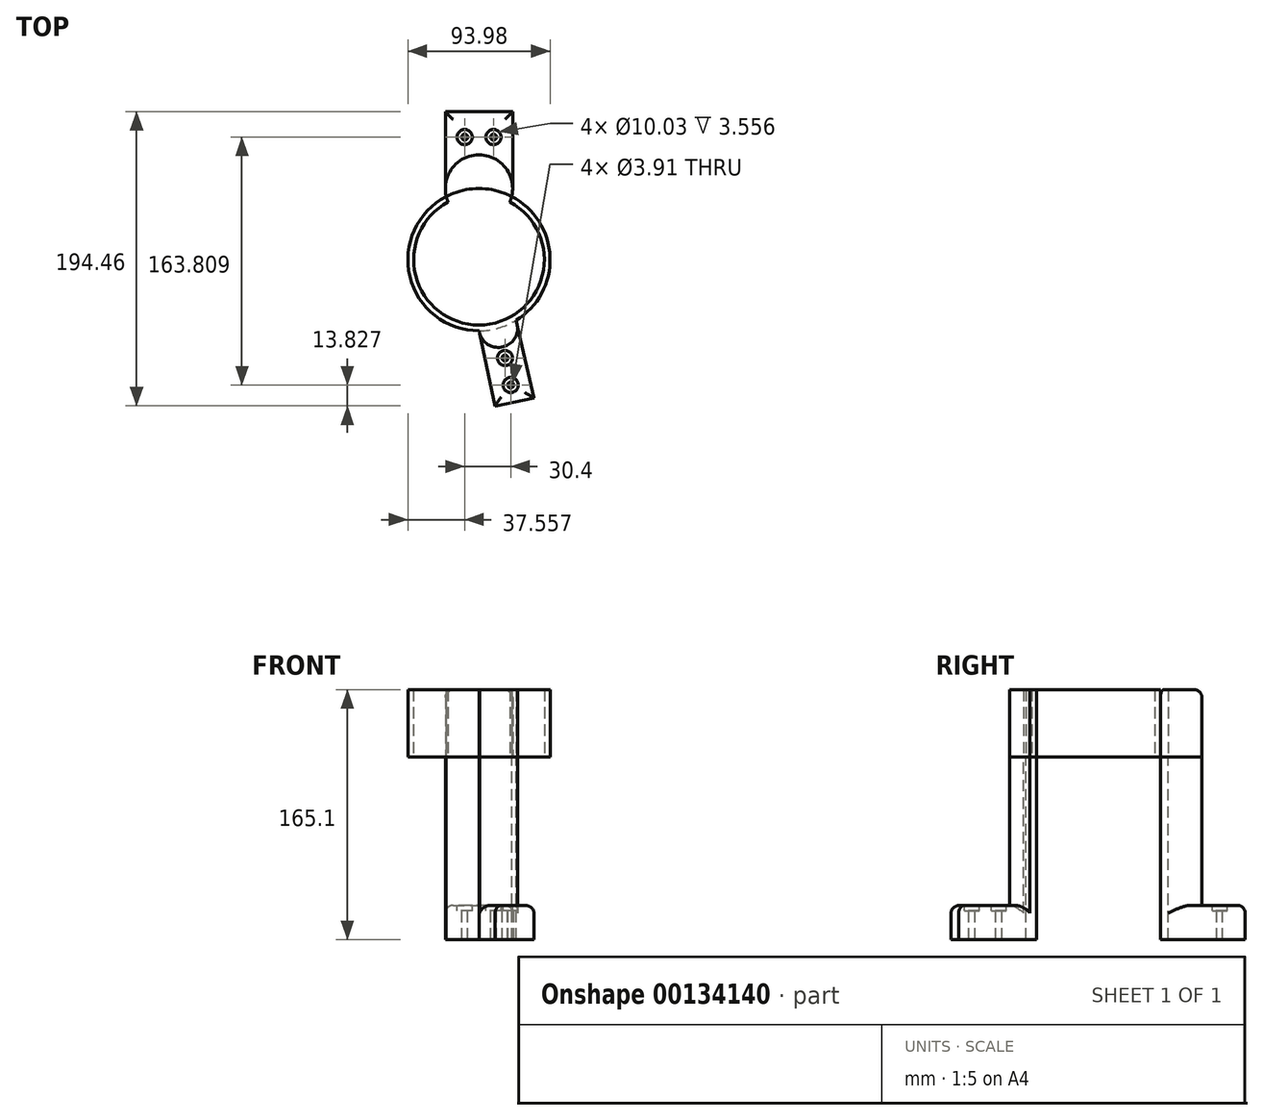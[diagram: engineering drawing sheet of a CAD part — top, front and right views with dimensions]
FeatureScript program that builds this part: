
annotation { "Feature Type Name" : "Feature", "Feature Type Description" : "" }
export const myFeature = defineFeature(function(context is Context, id is Id, definition is map)
    precondition{}
    {
        {
            var Q0;
            Q0=qCreatedBy(makeId("Top.planeOp"),FACE);
            var sketch = newSketch(context, id + "F0", { "sketchPlane" : qUnion([Q0])});
            skCircle(sketch, "E0", {"center": v(0, 0) * mm, "radius": 43.18 * mm});
            skCircle(sketch, "E1", {"center": v(0, 0) * mm, "radius": 47 * mm});
            skArc(sketch, "E2", {"start": v(0.07, -46.99) * mm, "mid": v(16.21, -57.54) * mm, "end": v(24.47, -40.11) * mm});
            skPoint(sketch, "E3.center.orphan", {"position": v(0, 47) * mm});
            skArc(sketch, "E4", {"start": v(0.12, -43.18) * mm, "mid": v(16.21, -57.54) * mm, "end": v(22.45, -36.89) * mm});
            skLineSegment(sketch, "E5", {"start": v(0.07, -46.99) * mm, "end": v(10.67, -96.67) * mm});
            skLineSegment(sketch, "E6", {"start": v(36.38, -91.59) * mm, "end": v(24.47, -40.11) * mm});
            skArc(sketch, "E7", {"start": v(20.36, 38.08) * mm, "mid": v(0, 69.22) * mm, "end": v(-20.36, 38.08) * mm});
            skLineSegment(sketch, "E8", {"start": v(-22.23, 47) * mm, "end": v(-22.23, 97.8) * mm});
            skLineSegment(sketch, "E9", {"start": v(-22.23, 97.8) * mm, "end": v(22.23, 97.8) * mm});
            skLineSegment(sketch, "E10", {"start": v(22.23, 97.8) * mm, "end": v(22.22, 46.99) * mm});
            skLineSegment(sketch, "E11", {"start": v(10.67, -96.67) * mm, "end": v(36.38, -91.59) * mm});
            skCircle(sketch, "E12", {"center": v(17.2, -64.98) * mm, "radius": 5.02 * mm});
            skCircle(sketch, "E13", {"center": v(20.97, -82.84) * mm, "radius": 5.02 * mm});
            skCircle(sketch, "E14", {"center": v(-9.43, 80.97) * mm, "radius": 5.02 * mm});
            skCircle(sketch, "E15.1.0.0", {"center": v(9.62, 80.97) * mm, "radius": 5.02 * mm});
            skLineSegment(sketch, "E15.direction1", {"start": v(-9.43, 80.97) * mm, "end": v(9.62, 80.97) * mm, "construction": true});
            skCircle(sketch, "E16", {"center": v(-9.43, 80.97) * mm, "radius": 1.96 * mm});
            skCircle(sketch, "E17", {"center": v(9.62, 80.97) * mm, "radius": 1.96 * mm});
            skCircle(sketch, "E18", {"center": v(17.2, -64.98) * mm, "radius": 1.96 * mm});
            skCircle(sketch, "E19", {"center": v(20.97, -82.84) * mm, "radius": 1.96 * mm});
            skSolve(sketch);
        }
        {
            var Q0;
            {var subQ0=sQuery(id+"F0.wireOp",EDGE,"E4");var subQ1=sQuery(id+"F0.wireOp",EDGE,"E1");var subQ2=makeQuery(id+"F0.imprint","INTERSECT",VERTEX,{"disambiguationData":[OD(0.0)],"derivedFrom":[subQ1,subQ0]});Q0=makeQuery(id+"F0.imprint","IMPRINT",FACE,{"disambiguationData":[TD([[makeQuery(id+"F0.imprint","IMPRINT",EDGE,{"disambiguationData":[TD([[subQ2,-1.0]])],"derivedFrom":subQ1}),-1.0]])]});}
            var Q1;
            {var subQ0=sQuery(id+"F0.wireOp",EDGE,"XKigaTq3-lD6u-q0mf-ILFs-nLOiHahSTtli");var subQ1=sQuery(id+"F0.wireOp",EDGE,"E1");var subQ2=makeQuery(id+"F0.imprint","INTERSECT",VERTEX,{"disambiguationData":[OD(0.0)],"derivedFrom":[subQ1,subQ0]});Q1=makeQuery(id+"F0.imprint","IMPRINT",FACE,{"disambiguationData":[TD([[makeQuery(id+"F0.imprint","IMPRINT",EDGE,{"disambiguationData":[TD([[subQ2,1.0]])],"derivedFrom":subQ1}),-1.0]])]});}
            extrude(context, id + "F1", {"entities" : qUnion([Q0, Q1]), "oppositeDirection" : true, "depth" : 120.65 * mm});
        }
        {
            var Q0;
            {var subQ0=sQuery(id+"F0.wireOp",EDGE,"E4");var subQ1=sQuery(id+"F0.wireOp",EDGE,"E0");var subQ2=makeQuery(id+"F0.imprint","INTERSECT",VERTEX,{"disambiguationData":[OD(1.0)],"derivedFrom":[subQ1,subQ0]});Q0=makeQuery(id+"F0.imprint","IMPRINT",FACE,{"disambiguationData":[TD([[makeQuery(id+"F0.imprint","IMPRINT",EDGE,{"disambiguationData":[TD([[subQ2,-1.0]])],"derivedFrom":subQ1}),-1.0]])]});}
            var Q1;
            {var subQ0=sQuery(id+"F0.wireOp",EDGE,"E4");var subQ1=sQuery(id+"F0.wireOp",EDGE,"E0");var subQ2=makeQuery(id+"F0.imprint","INTERSECT",VERTEX,{"disambiguationData":[OD(0.0)],"derivedFrom":[subQ1,subQ0]});Q1=makeQuery(id+"F0.imprint","IMPRINT",FACE,{"disambiguationData":[TD([[makeQuery(id+"F0.imprint","IMPRINT",EDGE,{"disambiguationData":[TD([[subQ2,-1.0]])],"derivedFrom":subQ1}),-1.0]])]});}
            var Q2;
            {var subQ0=sQuery(id+"F0.wireOp",EDGE,"E4");var subQ1=sQuery(id+"F0.wireOp",EDGE,"E0");var subQ2=makeQuery(id+"F0.imprint","INTERSECT",VERTEX,{"disambiguationData":[OD(0.0)],"derivedFrom":[subQ1,subQ0]});Q2=makeQuery(id+"F0.imprint","IMPRINT",FACE,{"disambiguationData":[TD([[makeQuery(id+"F0.imprint","IMPRINT",EDGE,{"disambiguationData":[TD([[subQ2,1.0]])],"derivedFrom":subQ1}),-1.0]])]});}
            var Q3;
            {var subQ0=sQuery(id+"F0.wireOp",EDGE,"XKigaTq3-lD6u-q0mf-ILFs-nLOiHahSTtli");var subQ1=sQuery(id+"F0.wireOp",EDGE,"E0");var subQ2=makeQuery(id+"F0.imprint","INTERSECT",VERTEX,{"disambiguationData":[OD(0.0)],"derivedFrom":[subQ1,subQ0]});Q3=makeQuery(id+"F0.imprint","IMPRINT",FACE,{"disambiguationData":[TD([[makeQuery(id+"F0.imprint","IMPRINT",EDGE,{"disambiguationData":[TD([[subQ2,-1.0]])],"derivedFrom":subQ1}),-1.0]])]});}
            var Q4;
            {var subQ0=sQuery(id+"F0.wireOp",EDGE,"XKigaTq3-lD6u-q0mf-ILFs-nLOiHahSTtli");var subQ1=sQuery(id+"F0.wireOp",EDGE,"E1");var subQ2=makeQuery(id+"F0.imprint","INTERSECT",VERTEX,{"disambiguationData":[OD(0.0)],"derivedFrom":[subQ1,subQ0]});Q4=makeQuery(id+"F0.imprint","IMPRINT",FACE,{"disambiguationData":[TD([[makeQuery(id+"F0.imprint","IMPRINT",EDGE,{"disambiguationData":[TD([[subQ2,1.0]])],"derivedFrom":subQ1}),-1.0]])]});}
            var Q5;
            {var subQ0=sQuery(id+"F0.wireOp",EDGE,"E4");var subQ1=sQuery(id+"F0.wireOp",EDGE,"E1");var subQ2=makeQuery(id+"F0.imprint","INTERSECT",VERTEX,{"disambiguationData":[OD(0.0)],"derivedFrom":[subQ1,subQ0]});Q5=makeQuery(id+"F0.imprint","IMPRINT",FACE,{"disambiguationData":[TD([[makeQuery(id+"F0.imprint","IMPRINT",EDGE,{"disambiguationData":[TD([[subQ2,-1.0]])],"derivedFrom":subQ1}),-1.0]])]});}
            extrude(context, id + "F2", {"entities" : qUnion([Q0, Q1, Q2, Q3, Q4, Q5]), "depth" : 44.45 * mm});
        }
        {
            var Q0;
            {var subQ0=sQuery(id+"F0.wireOp",EDGE,"E11");Q0=makeQuery(id+"F0.imprint","IMPRINT",FACE,{"disambiguationData":[TD([[makeQuery(id+"F0.imprint","IMPRINT",EDGE,{"derivedFrom":subQ0}),1.0]])]});}
            extrude(context, id + "F3", {"entities" : qUnion([Q0]), "operationType" : NewBodyOperationType.ADD, "oppositeDirection" : true, "depth" : 120.65 * mm, "hasSecondDirection" : true, "secondDirectionOppositeDirection" : true, "secondDirectionDepth" : 98.04 * mm});
        }
        {
            var Q0;
            {var subQ1=sQuery(id+"F0.wireOp",EDGE,"E8");Q0=makeQuery(id+"F0.imprint","IMPRINT",FACE,{"disambiguationData":[TD([[makeQuery(id+"F0.imprint","IMPRINT",EDGE,{"derivedFrom":subQ1}),-1.0]])]});}
            extrude(context, id + "F4", {"entities" : qUnion([Q0]), "operationType" : NewBodyOperationType.ADD, "oppositeDirection" : true, "depth" : 120.65 * mm, "hasSecondDirection" : true, "secondDirectionOppositeDirection" : true, "secondDirectionDepth" : 98.04 * mm});
        }
        {
            var Q0;
            Q0=makeQuery(id+"F0.imprint","IMPRINT",FACE,{"disambiguationData":[TD([[makeQuery(id+"F0.imprint","IMPRINT",EDGE,{"derivedFrom":sQuery(id+"F0.wireOp",EDGE,"E14")}),1.0]])]});
            extrude(context, id + "F5", {"entities" : qUnion([Q0]), "operationType" : NewBodyOperationType.ADD, "oppositeDirection" : true, "depth" : 120.65 * mm, "hasSecondDirection" : true, "secondDirectionOppositeDirection" : true, "secondDirectionDepth" : 101.6 * mm});
        }
        {
            var Q0;
            Q0=makeQuery(id+"F0.imprint","IMPRINT",FACE,{"disambiguationData":[TD([[makeQuery(id+"F0.imprint","IMPRINT",EDGE,{"derivedFrom":sQuery(id+"F0.wireOp",EDGE,"E15.1.0.0")}),1.0]])]});
            extrude(context, id + "F6", {"entities" : qUnion([Q0]), "operationType" : NewBodyOperationType.ADD, "oppositeDirection" : true, "depth" : 120.65 * mm, "hasSecondDirection" : true, "secondDirectionOppositeDirection" : true, "secondDirectionDepth" : 101.6 * mm});
        }
        {
            var Q0;
            Q0=makeQuery(id+"F0.imprint","IMPRINT",FACE,{"disambiguationData":[TD([[makeQuery(id+"F0.imprint","IMPRINT",EDGE,{"derivedFrom":sQuery(id+"F0.wireOp",EDGE,"E12")}),1.0]])]});
            extrude(context, id + "F7", {"entities" : qUnion([Q0]), "operationType" : NewBodyOperationType.ADD, "oppositeDirection" : true, "depth" : 120.65 * mm, "hasSecondDirection" : true, "secondDirectionOppositeDirection" : true, "secondDirectionDepth" : 101.6 * mm});
        }
        {
            var Q0;
            Q0=makeQuery(id+"F0.imprint","IMPRINT",FACE,{"disambiguationData":[TD([[makeQuery(id+"F0.imprint","IMPRINT",EDGE,{"derivedFrom":sQuery(id+"F0.wireOp",EDGE,"E13")}),1.0]])]});
            extrude(context, id + "F8", {"entities" : qUnion([Q0]), "operationType" : NewBodyOperationType.ADD, "oppositeDirection" : true, "depth" : 120.65 * mm, "hasSecondDirection" : true, "secondDirectionOppositeDirection" : true, "secondDirectionDepth" : 101.6 * mm});
        }
        {
            var Q0;
            {var subQ0=sQuery(id+"F0.wireOp",EDGE,"E1");Q0=makeQuery(id+"F2.opExtrude","CAP_EDGE",EDGE,{"disambiguationData":[OSD([subQ0]),TDD([makeQuery(id+"F0.imprint","IMPRINT",EDGE,{"disambiguationData":[TD([[makeQuery(id+"F0.imprint","INTERSECT",VERTEX,{"disambiguationData":[OD(0.0)],"derivedFrom":[subQ0,sQuery(id+"F0.wireOp",EDGE,"E7")]}),-1.0]])],"derivedFrom":subQ0})])],"isStart":false});}
            var Q1;
            Q1=makeQuery(id+"F2.opExtrude","CAP_EDGE",EDGE,{"disambiguationData":[OSD([sQuery(id+"F0.wireOp",EDGE,"E4")])],"isStart":false});
            var Q2;
            Q2=makeQuery(id+"F2.opExtrude","CAP_EDGE",EDGE,{"disambiguationData":[OSD([sQuery(id+"F0.wireOp",EDGE,"E6")])],"isStart":false});
            var Q3;
            Q3=makeQuery(id+"F2.opExtrude","CAP_EDGE",EDGE,{"disambiguationData":[OSD([sQuery(id+"F0.wireOp",EDGE,"E5")])],"isStart":false});
            var Q4;
            {var subQ0=sQuery(id+"F0.wireOp",EDGE,"E1");Q4=makeQuery(id+"F2.opExtrude","CAP_EDGE",EDGE,{"disambiguationData":[OSD([subQ0]),TDD([makeQuery(id+"F0.imprint","IMPRINT",EDGE,{"disambiguationData":[TD([[makeQuery(id+"F0.imprint","INTERSECT",VERTEX,{"disambiguationData":[OD(1.0)],"derivedFrom":[subQ0,sQuery(id+"F0.wireOp",EDGE,"E7")]}),1.0]])],"derivedFrom":subQ0})])],"isStart":false});}
            var Q5;
            Q5=makeQuery(id+"F2.opExtrude","CAP_EDGE",EDGE,{"disambiguationData":[OSD([sQuery(id+"F0.wireOp",EDGE,"E7")])],"isStart":false});
            fillet(context, id + "F9", {"entities" : qUnion([Q0, Q1, Q2, Q3, Q4, Q5]), "radius" : 5.08 * mm, "tangentPropagation" : true, "allowEdgeOverflow" : false});
        }
        {
            var Q0;
            Q0=makeQuery(id+"F3.opExtrude","CAP_EDGE",EDGE,{"disambiguationData":[OSD([sQuery(id+"F0.wireOp",EDGE,"E5")])],"isStart":true});
            var Q1;
            Q1=makeQuery(id+"F3.opExtrude","CAP_EDGE",EDGE,{"disambiguationData":[OSD([sQuery(id+"F0.wireOp",EDGE,"E11")])],"isStart":true});
            var Q2;
            Q2=makeQuery(id+"F3.opExtrude","CAP_EDGE",EDGE,{"disambiguationData":[OSD([sQuery(id+"F0.wireOp",EDGE,"E6")])],"isStart":true});
            fillet(context, id + "F10", {"entities" : qUnion([Q0, Q1, Q2]), "radius" : 5.08 * mm, "tangentPropagation" : true, "allowEdgeOverflow" : false});
        }
        {
            var Q0;
            Q0=makeQuery(id+"F4.opExtrude","CAP_EDGE",EDGE,{"disambiguationData":[OSD([sQuery(id+"F0.wireOp",EDGE,"E8")])],"isStart":true});
            var Q1;
            Q1=makeQuery(id+"F4.opExtrude","CAP_EDGE",EDGE,{"disambiguationData":[OSD([sQuery(id+"F0.wireOp",EDGE,"E9")])],"isStart":true});
            var Q2;
            Q2=makeQuery(id+"F4.opExtrude","CAP_EDGE",EDGE,{"disambiguationData":[OSD([sQuery(id+"F0.wireOp",EDGE,"E10")])],"isStart":true});
            fillet(context, id + "F11", {"entities" : qUnion([Q0, Q1, Q2]), "radius" : 5.08 * mm, "tangentPropagation" : true, "allowEdgeOverflow" : false});
        }
    });
